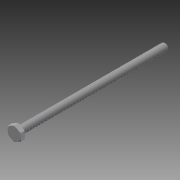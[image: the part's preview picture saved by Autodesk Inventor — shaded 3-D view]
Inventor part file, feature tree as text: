
AUTODESK INVENTOR PART (.ipt)
format: ipt  version: 2014 SP1 (Build 180222100, 222)  size: 1,564,672 bytes
history: native  units: in
note: dims shown in document units (in); Inventor stores cm internally (conversion verified against a paired STEP export)
features: extrude x1, other x1, imported_body x1
ambient origin geometry x8: Origin, YZ Plane, XZ Plane, XY Plane, X Axis, Y Axis, Z Axis, Center Point
bodies: Body1 (feature_tree)
feature tree (3):
  extrude  "Extrude14"  [1 undecoded]
  other  "92620A5571"
  imported_body  "Base1"
note: 1 required parameter value undecoded (feature->parameter linkage not recoverable at this tier; creation-order binding heuristic only, values carry confidence <= 0.55)
